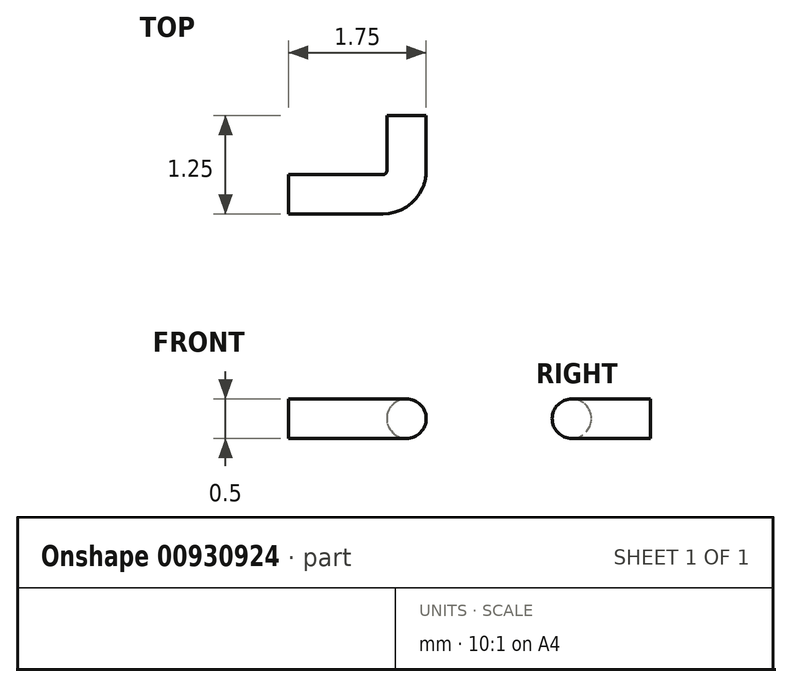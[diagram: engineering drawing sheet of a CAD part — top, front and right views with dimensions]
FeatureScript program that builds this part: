
annotation { "Feature Type Name" : "Feature", "Feature Type Description" : "" }
export const myFeature = defineFeature(function(context is Context, id is Id, definition is map)
    precondition{}
    {
        {
            var Q0;
            Q0=qCreatedBy(makeId("Right.planeOp"),FACE);
            var sketch = newSketch(context, id + "F0", { "sketchPlane" : qUnion([Q0])});
            skCircle(sketch, "E0", {"center": v(0, 0) * mm, "radius": 0.25 * mm});
            skSolve(sketch);
        }
        {
            var Q0;
            Q0=qCreatedBy(makeId("Top.planeOp"),FACE);
            var sketch = newSketch(context, id + "F1", { "sketchPlane" : qUnion([Q0])});
            skLineSegment(sketch, "E1", {"start": v(0, 0) * mm, "end": v(1.2, 0) * mm});
            skLineSegment(sketch, "E2", {"start": v(1.5, 0.3) * mm, "end": v(1.5, 1) * mm});
            skPoint(sketch, "E3.visualSharp", {"position": v(1.5, 0) * mm});
            skArc(sketch, "E3.filletArc", {"start": v(1.2, 0) * mm, "mid": v(1.41, 0.09) * mm, "end": v(1.5, 0.3) * mm});
            skSolve(sketch);
        }
        {
            var Q0;
            Q0 = qSketchRegion(id + "F0", true);
            var Q1;
            Q1 = qBodyType(qCreatedBy(id + "F1" ,EDGE), BodyType.WIRE);
            sweep(context, id + "F2", {"profiles" : qUnion([Q0]), "path" : qUnion([Q1])});
        }
    });
